# Revit family: Domotics-SerieCivili-GEWISS-27COMBI_SYSTEM-IP40_PRESA_ITA_GER
name_source: partatom
category: Apparecchi elettrici
revit_build: Autodesk Revit 2016 (Build: 20161004_0715(x64)
units: mm (PartAtom-declared; Revit-internal decimal feet)

## family parameters
Condiviso = Sì
Host = Superficie
Mantenere orientamento annotazione = Sì
Numero OmniClass = 23.80.50.14
Punto di calcolo locali = No
Quota connettore circolare = Usa diametro
Taglio con vuoti quando caricato = Sì
Tipo di parte = Normale
Titolo OmniClass = Plug Connectors

## types (1)
- Domotics-SerieCivili-GEWISS-27COMBI_SYSTEM-IP40_PRESA_ITA_GER
    Caratteristiche = Standard Italiano/Tedesco
    Catalogo = DOMOTICS
    Catalogo Serie = 27COMBI
    Classe isolamento = II
    Codice EAN = 8011564095403
    Codice Electrocod = 0131
    Colore = Grigio RAL 7035
    Coppia serraggio viti = 0,8NM
    Descrizione = PRESA STD ITA./TED.2P+T 16A BIV.PROTETTA
    Descrizione: = Presa 2P+T - 16 A bivalente
    Dim. esterne BxHxP (mm) = 66x82x55
    Dimensioni BxHxP (mm) = 66x82x55
    GW - Testo elettrico = 10/16
    Glow Wire Test = 650°C
    Grado di protezione = IP40
    IDF = b8496a88-3aba-4f4e-bde3-e91454acf831
    IDT = 02c93d32-6b55-41be-8c82-e1a355b4a134
    Immagine tipo = GW27812.jpg
    Larghezza foro = 23 mm  [stored 0.0754593 ft]
    Larghezza scatola = 66 mm  [stored 0.216535 ft]
    Modello = GW27812
    N. fori Ã˜ 23 con passacavo = 1
    N. fori Ã˜ 23 sfondabili: = Laterali 3 / Sul fondo 1
    Norma di riferimento: = IEC 60884-1
    Produttore = GEWISS S.p.A.
    Prospetto di default = 1219 mm
    SCATOLA = GEWISS GRIGIO
    SEO = Contenitore
    Scheda Tecnica = https://www.gewiss.com
    Simbolo = SIMBOLO PRESE : PRESA
    Temperatura di installazione = -25 +60 °C
    Tensione = 230 V ac
    Tensione: = 250 V ac
    Termopressione con biglia = 70 °C
    Tipo sfondabili = Asportabili con utensile
    URL = https://www.gewiss.com
    Versione file RFA = 19.4
    Viti coperchio = Acciaio resistente alla corrosione

note: [stored X ft] marks values corroborated as IEEE doubles in the binary element streams (Revit-internal decimal feet)

## geometry (parser evidence)
native form markers: Sweep x2
no freeform markers — native parametric forms only
